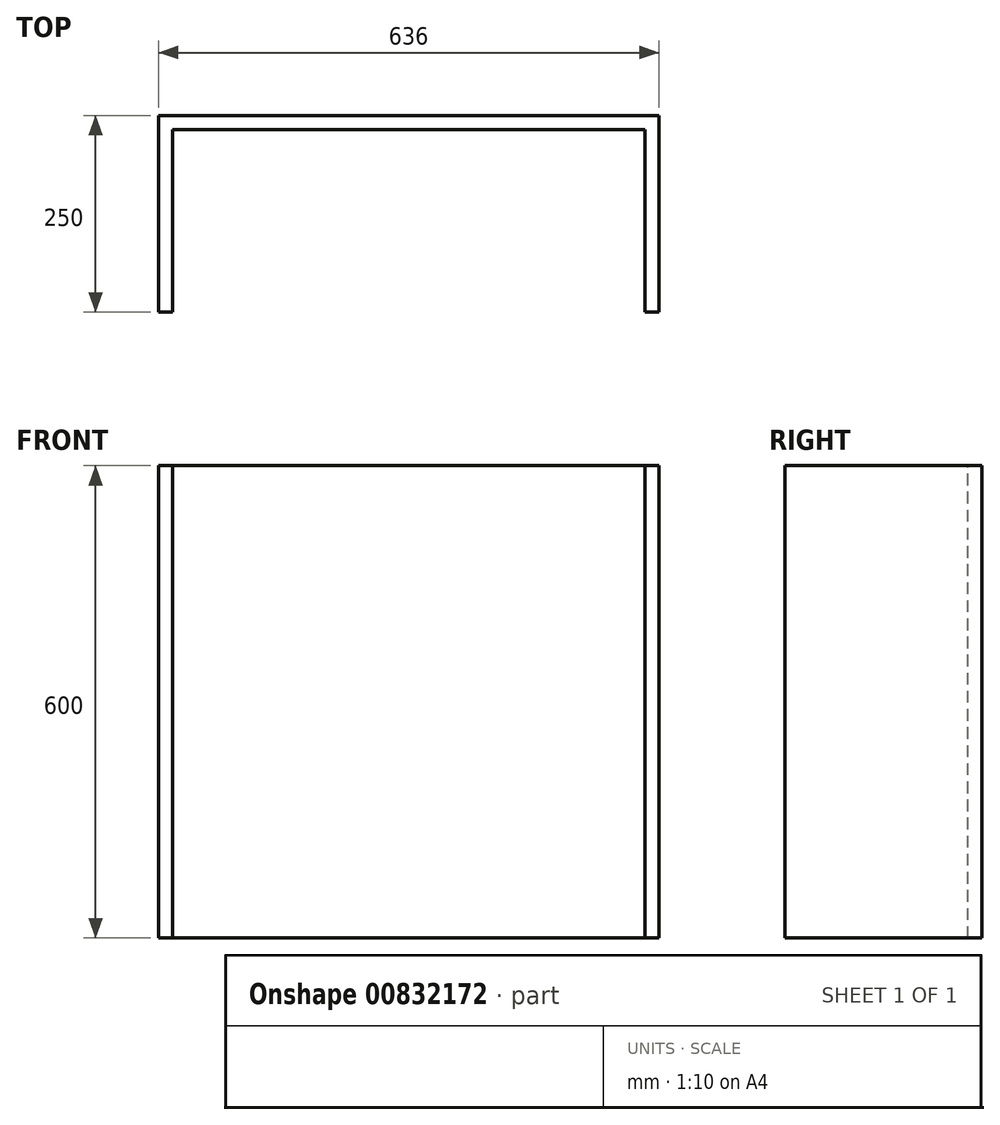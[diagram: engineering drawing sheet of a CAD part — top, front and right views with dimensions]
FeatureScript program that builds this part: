
annotation { "Feature Type Name" : "Feature", "Feature Type Description" : "" }
export const myFeature = defineFeature(function(context is Context, id is Id, definition is map)
    precondition{}
    {
        {
            var Q0;
            Q0=qCreatedBy(makeId("Front.planeOp"),FACE);
            var sketch = newSketch(context, id + "F0", { "sketchPlane" : qUnion([Q0])});
            skLineSegment(sketch, "E0.bottom", {"start": v(300, -300) * mm, "end": v(-300, -300) * mm});
            skLineSegment(sketch, "E0.top", {"start": v(300, 300) * mm, "end": v(-300, 300) * mm});
            skLineSegment(sketch, "E0.left", {"start": v(300, -300) * mm, "end": v(300, 300) * mm});
            skLineSegment(sketch, "E0.right", {"start": v(-300, -300) * mm, "end": v(-300, 300) * mm});
            skPoint(sketch, "E0.middle", {"position": v(0, 0) * mm});
            skSolve(sketch);
        }
        {
            var Q0;
            Q0 = qSketchRegion(id + "F0", true);
            extrude(context, id + "F1", {"entities" : qUnion([Q0]), "depth" : 18 * mm, "offsetDistance" : 25 * mm});
        }
        {
            var Q0;
            Q0=qCreatedBy(makeId("Front.planeOp"),FACE);
            var sketch = newSketch(context, id + "F2", { "sketchPlane" : qUnion([Q0])});
            skLineSegment(sketch, "E1.bottom", {"start": v(-300, -300) * mm, "end": v(-318, -300) * mm});
            skLineSegment(sketch, "E1.top", {"start": v(-300, 300) * mm, "end": v(-318, 300) * mm});
            skLineSegment(sketch, "E1.left", {"start": v(-300, -300) * mm, "end": v(-300, 300) * mm});
            skLineSegment(sketch, "E1.right", {"start": v(-318, -300) * mm, "end": v(-318, 300) * mm});
            skSolve(sketch);
        }
        {
            var Q0;
            Q0=makeQuery(id+"F2.imprint","IMPRINT",FACE,{"disambiguationData":[TD([[makeQuery(id+"F2.imprint","IMPRINT",EDGE,{"derivedFrom":sQuery(id+"F2.wireOp",EDGE,"E1.bottom")}),-1.0]])]});
            extrude(context, id + "F3", {"entities" : qUnion([Q0]), "operationType" : NewBodyOperationType.ADD, "depth" : 250 * mm, "offsetDistance" : 25 * mm});
        }
        {
            var Q0;
            Q0=qCreatedBy(makeId("Front.planeOp"),FACE);
            var sketch = newSketch(context, id + "F4", { "sketchPlane" : qUnion([Q0])});
            skLineSegment(sketch, "E2.bottom", {"start": v(300, 300) * mm, "end": v(318, 300) * mm});
            skLineSegment(sketch, "E2.top", {"start": v(300, -300) * mm, "end": v(318, -300) * mm});
            skLineSegment(sketch, "E2.left", {"start": v(300, 300) * mm, "end": v(300, -300) * mm});
            skLineSegment(sketch, "E2.right", {"start": v(318, 300) * mm, "end": v(318, -300) * mm});
            skSolve(sketch);
        }
        {
            var Q0;
            Q0 = qSketchRegion(id + "F4", true);
            extrude(context, id + "F5", {"entities" : qUnion([Q0]), "operationType" : NewBodyOperationType.ADD, "depth" : 250 * mm, "offsetDistance" : 25 * mm});
        }
    });
